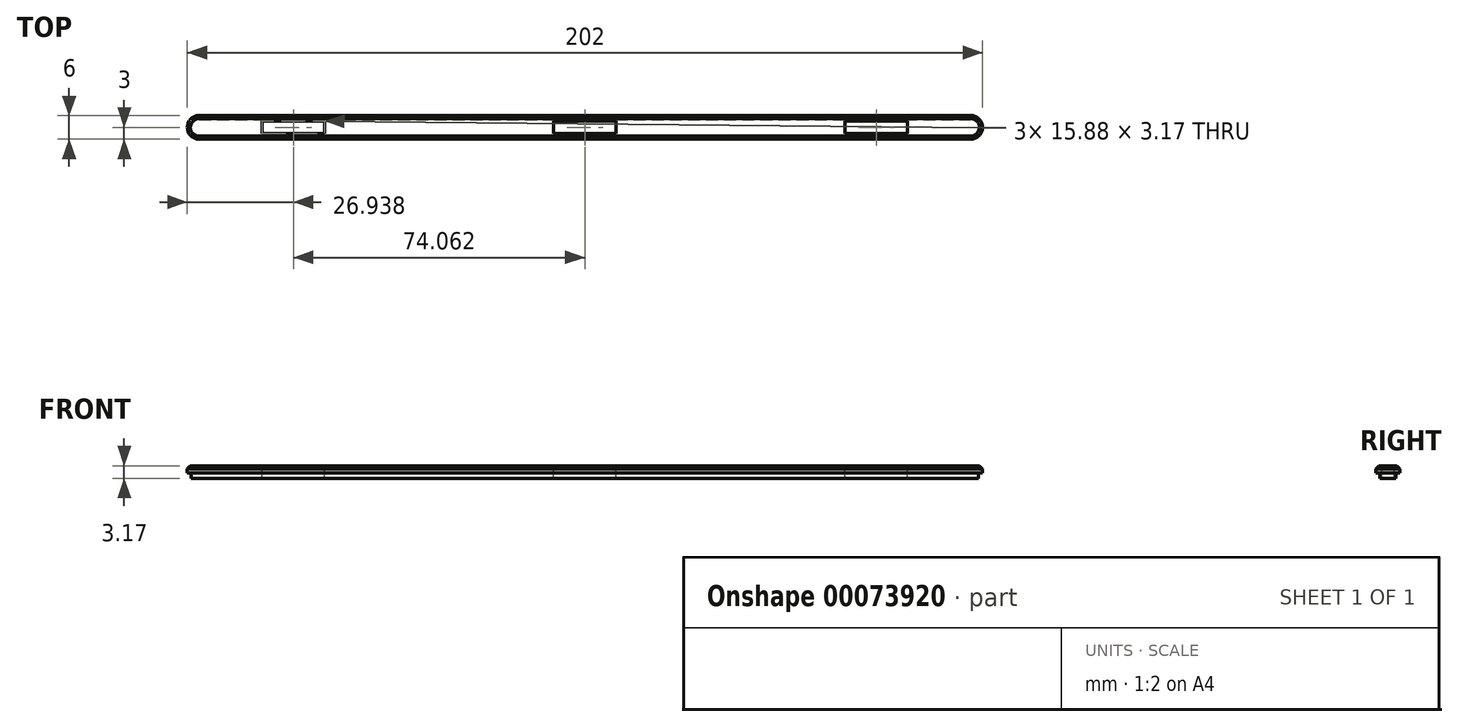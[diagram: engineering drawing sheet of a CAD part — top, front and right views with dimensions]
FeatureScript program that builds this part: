
annotation { "Feature Type Name" : "Feature", "Feature Type Description" : "" }
export const myFeature = defineFeature(function(context is Context, id is Id, definition is map)
    precondition{}
    {
        {
            var Q0;
            Q0=qCreatedBy(makeId("Top.planeOp"),FACE);
            var sketch = newSketch(context, id + "F0", { "sketchPlane" : qUnion([Q0])});
            skLineSegment(sketch, "E0", {"start": v(0, 0) * mm, "end": v(200, 0) * mm});
            skLineSegment(sketch, "E1", {"start": v(0, 0) * mm, "end": v(0, 4) * mm});
            skLineSegment(sketch, "E2", {"start": v(0, 4) * mm, "end": v(200, 4) * mm});
            skLineSegment(sketch, "E3", {"start": v(200, 4) * mm, "end": v(200, 0) * mm});
            skSolve(sketch);
        }
        {
            var Q0;
            Q0 = qSketchRegion(id + "F0", true);
            extrude(context, id + "F1", {"entities" : qUnion([Q0]), "depth" : 1.4 * mm});
        }
        {
            var Q0;
            Q0=makeQuery(id+"F1.opExtrude","SWEPT_EDGE",EDGE,{"disambiguationData":[OSD([sQuery(id+"F0.wireOp",EDGE,"E0"),sQuery(id+"F0.wireOp",EDGE,"E1")])]});
            var Q1;
            Q1=makeQuery(id+"F1.opExtrude","SWEPT_EDGE",EDGE,{"disambiguationData":[OSD([sQuery(id+"F0.wireOp",EDGE,"E1"),sQuery(id+"F0.wireOp",EDGE,"E2")])]});
            var Q2;
            Q2=makeQuery(id+"F1.opExtrude","SWEPT_EDGE",EDGE,{"disambiguationData":[OSD([sQuery(id+"F0.wireOp",EDGE,"E0"),sQuery(id+"F0.wireOp",EDGE,"E3")])]});
            var Q3;
            Q3=makeQuery(id+"F1.opExtrude","SWEPT_EDGE",EDGE,{"disambiguationData":[OSD([sQuery(id+"F0.wireOp",EDGE,"E2"),sQuery(id+"F0.wireOp",EDGE,"E3")])]});
            fillet(context, id + "F2", {"entities" : qUnion([Q0, Q1, Q2, Q3]), "radius" : 2 * mm, "tangentPropagation" : true, "allowEdgeOverflow" : false});
        }
        {
            var Q0;
            Q0=makeQuery(id+"F1.opExtrude","CAP_FACE",FACE,{"disambiguationData":[OSD([sQuery(id+"F0.wireOp",EDGE,"E0"),sQuery(id+"F0.wireOp",EDGE,"E1"),sQuery(id+"F0.wireOp",EDGE,"E2"),sQuery(id+"F0.wireOp",EDGE,"E3")])],"isStart":false});
            var sketch = newSketch(context, id + "F3", { "sketchPlane" : qUnion([Q0])});
            skLineSegment(sketch, "E4", {"start": v(0, 2) * mm, "end": v(18, 2) * mm, "construction": true});
            skLineSegment(sketch, "E5", {"start": v(200, 2) * mm, "end": v(182, 2) * mm, "construction": true});
            skLineSegment(sketch, "E6", {"start": v(18, 2) * mm, "end": v(18, 0.41) * mm});
            skLineSegment(sketch, "E7", {"start": v(18, 0.41) * mm, "end": v(33.88, 0.41) * mm});
            skLineSegment(sketch, "E8", {"start": v(33.88, 0.41) * mm, "end": v(33.88, 3.59) * mm});
            skLineSegment(sketch, "E9", {"start": v(33.88, 3.59) * mm, "end": v(18, 3.59) * mm});
            skLineSegment(sketch, "E10", {"start": v(18, 3.59) * mm, "end": v(18, 2) * mm});
            skLineSegment(sketch, "E11", {"start": v(182, 2) * mm, "end": v(182, 3.59) * mm});
            skLineSegment(sketch, "E12", {"start": v(182, 3.59) * mm, "end": v(166.12, 3.59) * mm});
            skLineSegment(sketch, "E13", {"start": v(166.12, 3.59) * mm, "end": v(166.12, 0.41) * mm});
            skLineSegment(sketch, "E14", {"start": v(166.12, 0.41) * mm, "end": v(182, 0.41) * mm});
            skLineSegment(sketch, "E15", {"start": v(182, 0.41) * mm, "end": v(182, 2) * mm});
            skLineSegment(sketch, "E16", {"start": v(100, 4) * mm, "end": v(100, 0) * mm, "construction": true});
            skLineSegment(sketch, "E17", {"start": v(100, 2) * mm, "end": v(92.06, 2) * mm, "construction": true});
            skLineSegment(sketch, "E18", {"start": v(92.06, 2) * mm, "end": v(92.06, 3.59) * mm});
            skLineSegment(sketch, "E19", {"start": v(92.06, 3.59) * mm, "end": v(107.94, 3.59) * mm});
            skLineSegment(sketch, "E20", {"start": v(107.94, 3.59) * mm, "end": v(107.94, 0.41) * mm});
            skLineSegment(sketch, "E21", {"start": v(107.94, 0.41) * mm, "end": v(92.06, 0.41) * mm});
            skLineSegment(sketch, "E22", {"start": v(92.06, 0.41) * mm, "end": v(92.06, 2) * mm});
            skSolve(sketch);
        }
        {
            var Q0;
            Q0=makeQuery(id+"F3.imprint","IMPRINT",FACE,{"disambiguationData":[TD([[makeQuery(id+"F3.imprint","IMPRINT",EDGE,{"derivedFrom":sQuery(id+"F3.wireOp",EDGE,"E6")}),-1.0]])]});
            var sketch = newSketch(context, id + "F4", { "sketchPlane" : qUnion([Q0])});
            skLineSegment(sketch, "E23.0", {"start": v(2, 5) * mm, "end": v(198, 5) * mm});
            skArc(sketch, "E23.1", {"start": v(2, 5) * mm, "mid": v(-1, 2) * mm, "end": v(2, -1) * mm});
            skLineSegment(sketch, "E23.2", {"start": v(2, -1) * mm, "end": v(198, -1) * mm});
            skArc(sketch, "E23.3", {"start": v(198, -1) * mm, "mid": v(201, 2) * mm, "end": v(198, 5) * mm});
            skSolve(sketch);
        }
        {
            var Q0;
            Q0 = qSketchRegion(id + "F4", true);
            extrude(context, id + "F5", {"entities" : qUnion([Q0]), "operationType" : NewBodyOperationType.ADD, "depth" : 3.17 * mm - 1.4 * mm});
        }
        {
            var Q0;
            Q0=makeQuery(id+"F5.opExtrude","CAP_EDGE",EDGE,{"disambiguationData":[OSD([sQuery(id+"F4.wireOp",EDGE,"E23.1")])],"isStart":false});
            chamfer(context, id + "F6", {"entities" : qUnion([Q0]), "width" : .75 * mm, "tangentPropagation" : true});
        }
        {
            var Q0;
            Q0 = qSketchRegion(id + "F3", true);
            extrude(context, id + "F7", {"entities" : qUnion([Q0]), "operationType" : NewBodyOperationType.REMOVE, "oppositeDirection" : true, "depth" : 1.4 * mm, "hasSecondDirection" : true, "secondDirectionOppositeDirection" : false, "secondDirectionDepth" : 25 * mm});
        }
    });
